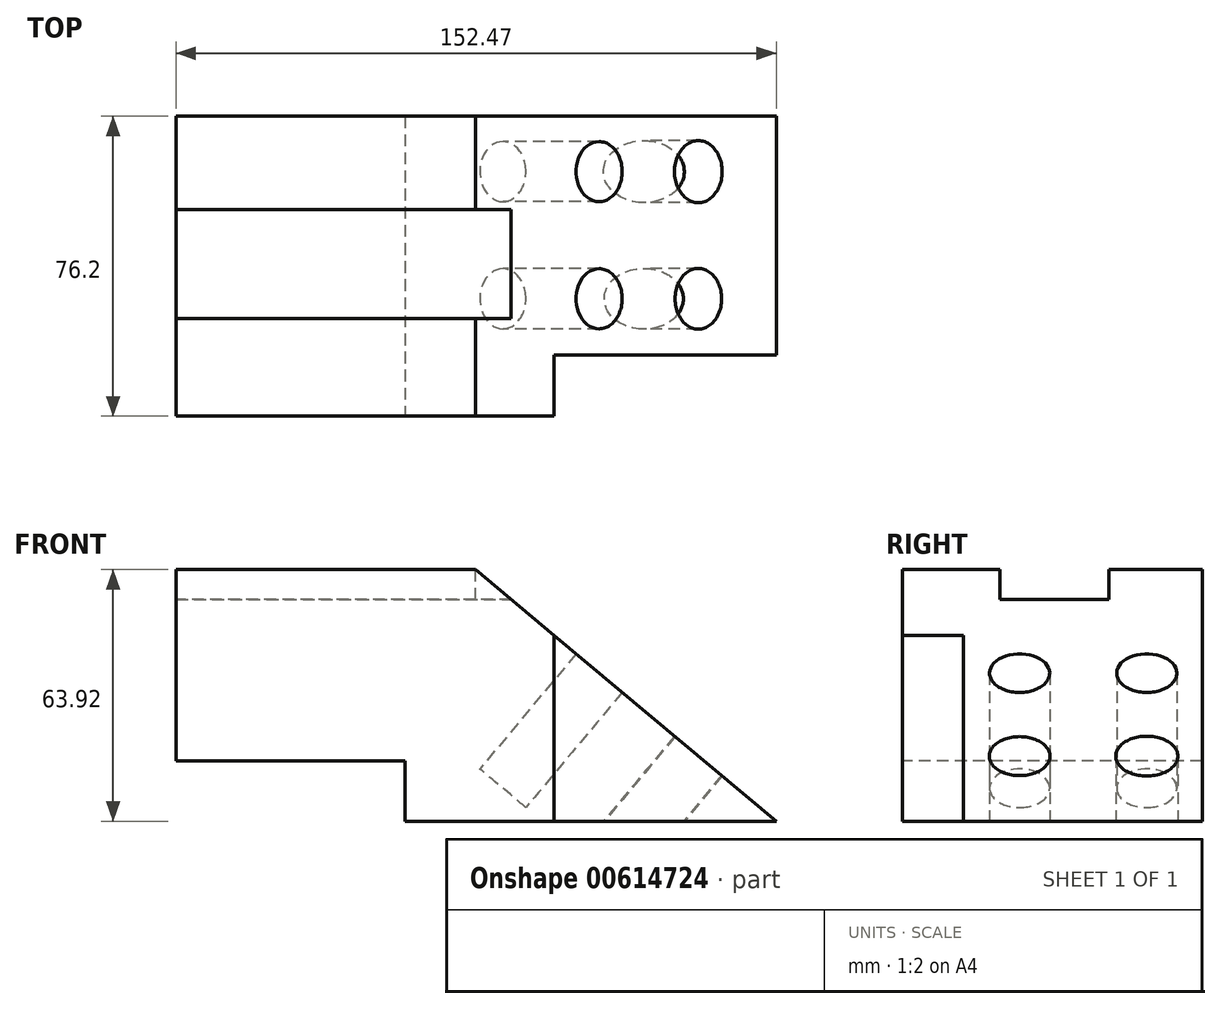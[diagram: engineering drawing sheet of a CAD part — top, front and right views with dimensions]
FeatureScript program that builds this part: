
annotation { "Feature Type Name" : "Feature", "Feature Type Description" : "" }
export const myFeature = defineFeature(function(context is Context, id is Id, definition is map)
    precondition{}
    {
        {
            var Q0;
            Q0=qCreatedBy(makeId("Front.planeOp"),FACE);
            var sketch = newSketch(context, id + "F0", { "sketchPlane" : qUnion([Q0])});
            skLineSegment(sketch, "E0", {"start": v(-76.01, 0) * mm, "end": v(-76.01, 63.92) * mm});
            skLineSegment(sketch, "E1", {"start": v(-76.01, 63.92) * mm, "end": v(0, 63.92) * mm});
            skLineSegment(sketch, "E2", {"start": v(0, 63.92) * mm, "end": v(76.46, 0) * mm});
            skLineSegment(sketch, "E3", {"start": v(76.46, 0) * mm, "end": v(0, 0) * mm});
            skLineSegment(sketch, "E4", {"start": v(0, 0) * mm, "end": v(-76.01, 0) * mm});
            skSolve(sketch);
        }
        {
            var Q0;
            Q0 = qSketchRegion(id + "F0", true);
            extrude(context, id + "F1", {"entities" : qUnion([Q0]), "endBound" : BoundingType.SYMMETRIC, "depth" : 76.2 * mm, "offsetDistance" : 25.4 * mm});
        }
        {
            var Q0;
            Q0=makeQuery(id+"F1.opExtrude","CAP_FACE",FACE,{"disambiguationData":[OSD([sQuery(id+"F0.wireOp",EDGE,"E0"),sQuery(id+"F0.wireOp",EDGE,"E1"),sQuery(id+"F0.wireOp",EDGE,"E2"),sQuery(id+"F0.wireOp",EDGE,"E3"),sQuery(id+"F0.wireOp",EDGE,"E4")])],"isStart":false});
            var sketch = newSketch(context, id + "F2", { "sketchPlane" : qUnion([Q0])});
            skLineSegment(sketch, "E5", {"start": v(-17.8, 0) * mm, "end": v(-17.8, 15.36) * mm});
            skLineSegment(sketch, "E6", {"start": v(-17.8, 15.36) * mm, "end": v(-76.01, 15.36) * mm});
            skLineSegment(sketch, "E7", {"start": v(-76.01, 15.36) * mm, "end": v(-76.01, 0) * mm});
            skLineSegment(sketch, "E8", {"start": v(-76.01, 0) * mm, "end": v(-17.8, 0) * mm});
            skSolve(sketch);
        }
        {
            var Q0;
            Q0 = qSketchRegion(id + "F2", true);
            extrude(context, id + "F3", {"entities" : qUnion([Q0]), "operationType" : NewBodyOperationType.REMOVE, "endBound" : BoundingType.SYMMETRIC, "oppositeDirection" : true, "depth" : 152.4 * mm, "offsetDistance" : 25.4 * mm});
        }
        {
            var Q0;
            Q0=qCreatedBy(makeId("Top.planeOp"),FACE);
            var sketch = newSketch(context, id + "F4", { "sketchPlane" : qUnion([Q0])});
            skLineSegment(sketch, "E9", {"start": v(19.97, -38.32) * mm, "end": v(19.97, -22.56) * mm});
            skLineSegment(sketch, "E10", {"start": v(19.97, -22.56) * mm, "end": v(76.51, -22.56) * mm});
            skLineSegment(sketch, "E11", {"start": v(76.51, -22.56) * mm, "end": v(76.51, -38.14) * mm});
            skLineSegment(sketch, "E12", {"start": v(76.51, -38.14) * mm, "end": v(19.97, -38.32) * mm});
            skSolve(sketch);
        }
        {
            var Q0;
            Q0 = qSketchRegion(id + "F4", true);
            extrude(context, id + "F5", {"entities" : qUnion([Q0]), "operationType" : NewBodyOperationType.REMOVE, "endBound" : BoundingType.SYMMETRIC, "depth" : 101.6 * mm, "offsetDistance" : 25.4 * mm});
        }
        {
            var Q0;
            Q0=makeQuery(id+"F1.opExtrude","SWEPT_FACE",FACE,{"disambiguationData":[OSD([sQuery(id+"F0.wireOp",EDGE,"E1")])]});
            var sketch = newSketch(context, id + "F6", { "sketchPlane" : qUnion([Q0])});
            skLineSegment(sketch, "E13", {"start": v(-76.01, -13.3) * mm, "end": v(0, -13.3) * mm});
            skLineSegment(sketch, "E14", {"start": v(0, -13.3) * mm, "end": v(0, 14.36) * mm});
            skLineSegment(sketch, "E15", {"start": v(0, 14.36) * mm, "end": v(-76.01, 14.36) * mm});
            skLineSegment(sketch, "E16", {"start": v(-76.01, 14.36) * mm, "end": v(-76.01, -13.3) * mm});
            skLineSegment(sketch, "E17", {"start": v(0, -13.3) * mm, "end": v(15.19, -13.3) * mm});
            skLineSegment(sketch, "E18", {"start": v(15.19, -13.3) * mm, "end": v(15.19, 14.52) * mm});
            skLineSegment(sketch, "E19", {"start": v(15.19, 14.52) * mm, "end": v(0, 14.36) * mm});
            skSolve(sketch);
        }
        {
            var Q0;
            Q0 = qSketchRegion(id + "F6", true);
            extrude(context, id + "F7", {"entities" : qUnion([Q0]), "operationType" : NewBodyOperationType.REMOVE, "oppositeDirection" : true, "depth" : 7.62 * mm, "offsetDistance" : 25.4 * mm});
        }
        {
            var Q0;
            Q0=makeQuery(id+"F1.opExtrude","SWEPT_FACE",FACE,{"disambiguationData":[OSD([sQuery(id+"F0.wireOp",EDGE,"E2")])]});
            var sketch = newSketch(context, id + "F8", { "sketchPlane" : qUnion([Q0])});
            skCircle(sketch, "E20", {"center": v(0, -8.27) * mm, "radius": 7.63 * mm});
            skCircle(sketch, "E21", {"center": v(32.86, -8.27) * mm, "radius": 7.71 * mm});
            skCircle(sketch, "E22", {"center": v(0, 24.03) * mm, "radius": 7.63 * mm});
            skCircle(sketch, "E23", {"center": v(32.86, 24.03) * mm, "radius": 7.89 * mm});
            skSolve(sketch);
        }
        {
            var Q0;
            Q0 = qSketchRegion(id + "F8", true);
            extrude(context, id + "F9", {"entities" : qUnion([Q0]), "operationType" : NewBodyOperationType.REMOVE, "endBound" : BoundingType.SYMMETRIC, "depth" : 76.2 * mm, "offsetDistance" : 25.4 * mm});
        }
    });
